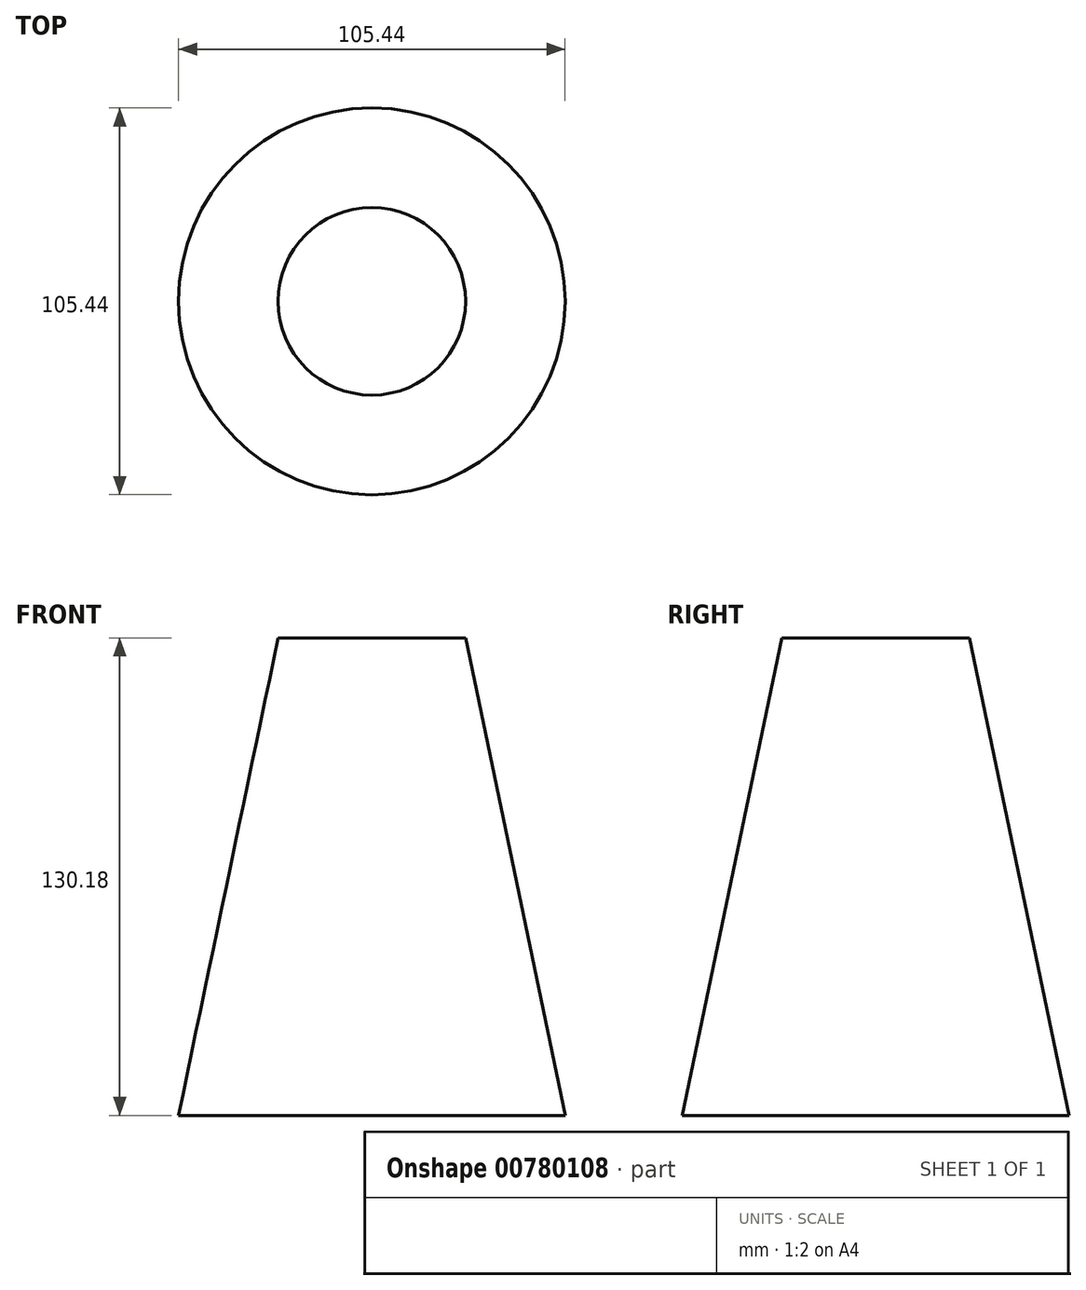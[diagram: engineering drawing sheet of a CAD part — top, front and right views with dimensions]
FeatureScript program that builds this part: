
annotation { "Feature Type Name" : "Feature", "Feature Type Description" : "" }
export const myFeature = defineFeature(function(context is Context, id is Id, definition is map)
    precondition{}
    {
        {
            var Q0;
            Q0=qCreatedBy(makeId("Front.planeOp"),FACE);
            var sketch = newSketch(context, id + "F0", { "sketchPlane" : qUnion([Q0])});
            skLineSegment(sketch, "E0", {"start": v(0, 0) * mm, "end": v(0, 130.18) * mm});
            skLineSegment(sketch, "E1", {"start": v(0, 130.18) * mm, "end": v(-25.56, 130.18) * mm});
            skLineSegment(sketch, "E2", {"start": v(-25.56, 130.18) * mm, "end": v(-52.72, 0) * mm});
            skLineSegment(sketch, "E3", {"start": v(-52.72, 0) * mm, "end": v(0, 0) * mm});
            skSolve(sketch);
        }
        {
            var Q0;
            Q0=makeQuery(id+"F0.imprint","IMPRINT",FACE,{"disambiguationData":[TD([[makeQuery(id+"F0.imprint","IMPRINT",EDGE,{"derivedFrom":sQuery(id+"F0.wireOp",EDGE,"E0")}),1.0]])]});
            var Q1;
            Q1=sQuery(id+"F0.wireOp",EDGE,"E0");
            revolve(context, id + "F1", {"surfaceOperationType" : NewSurfaceOperationType.NEW, "entities" : qUnion([Q0]), "axis" : qUnion([Q1]), "revolveType" : RevolveType.FULL});
        }
    });
